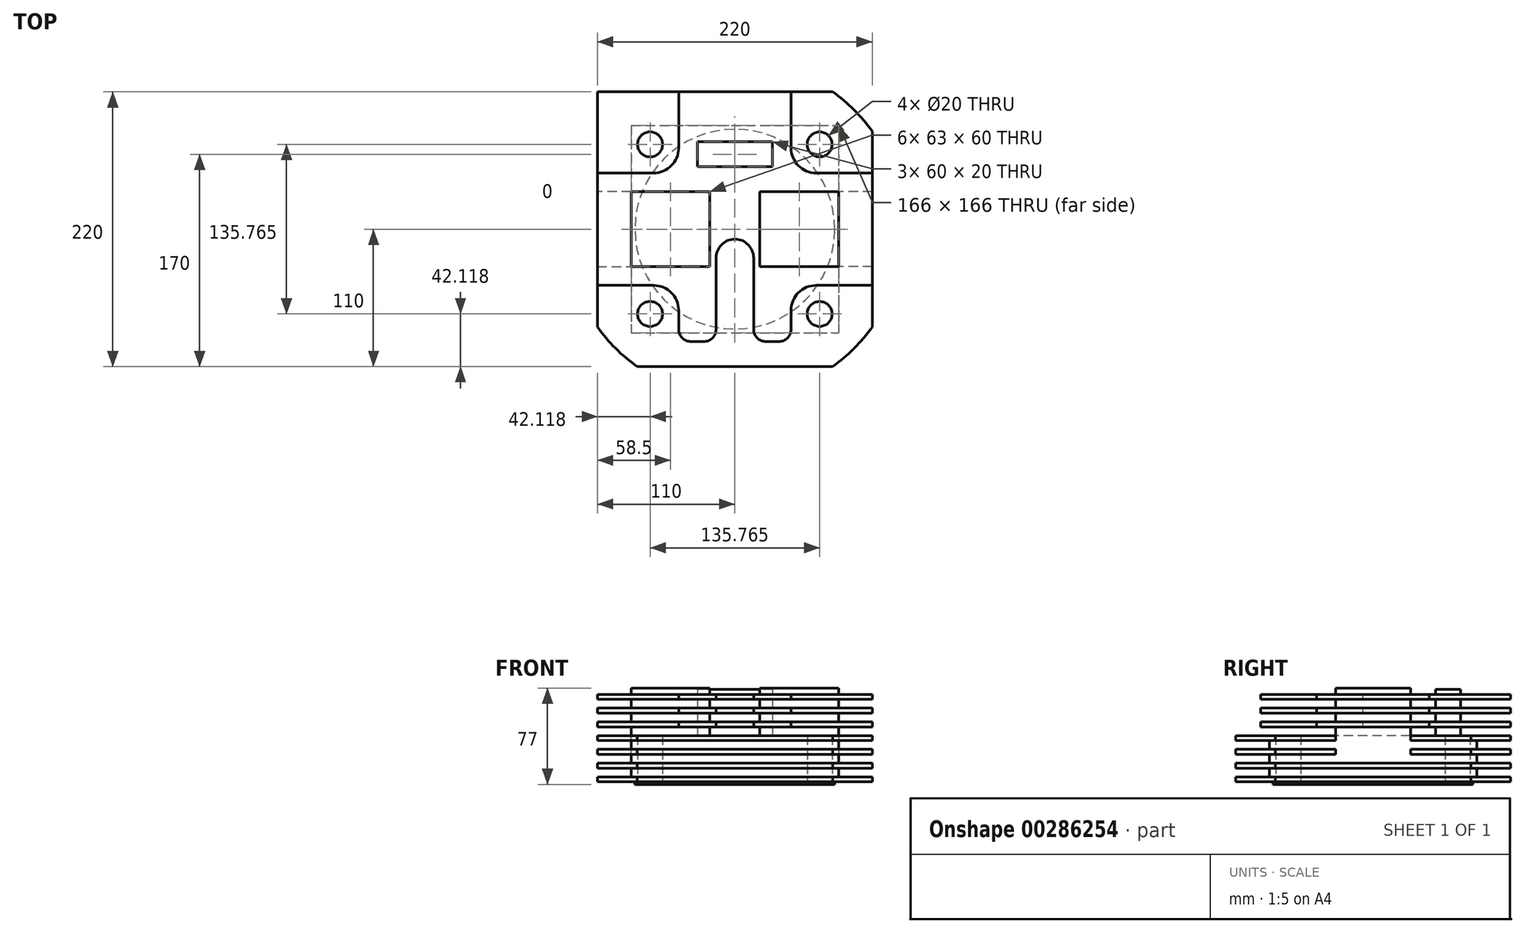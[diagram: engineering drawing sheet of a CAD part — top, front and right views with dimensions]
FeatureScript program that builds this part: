
annotation { "Feature Type Name" : "Feature", "Feature Type Description" : "" }
export const myFeature = defineFeature(function(context is Context, id is Id, definition is map)
    precondition{}
    {
        {
            var Q0;
            Q0=qCreatedBy(makeId("Top.planeOp"),FACE);
            var sketch = newSketch(context, id + "F0", { "sketchPlane" : qUnion([Q0])});
            skLineSegment(sketch, "E0.bottom", {"start": v(-110, 110) * mm, "end": v(110, 110) * mm});
            skLineSegment(sketch, "E0.top", {"start": v(-110, -110) * mm, "end": v(110, -110) * mm});
            skLineSegment(sketch, "E0.left", {"start": v(-110, 110) * mm, "end": v(-110, -110) * mm});
            skLineSegment(sketch, "E0.right", {"start": v(110, 110) * mm, "end": v(110, -110) * mm});
            skSolve(sketch);
        }
        {
            var Q0;
            Q0=makeQuery(id+"F0.imprint","IMPRINT",FACE,{"disambiguationData":[TD([[makeQuery(id+"F0.imprint","IMPRINT",EDGE,{"derivedFrom":sQuery(id+"F0.wireOp",EDGE,"E0.bottom")}),-1.0]])]});
            extrude(context, id + "F1", {"entities" : qUnion([Q0]), "depth" : 4 * mm});
        }
        {
            var Q0;
            Q0=makeQuery(id+"F1.opExtrude","CAP_FACE",FACE,{"disambiguationData":[OSD([sQuery(id+"F0.wireOp",EDGE,"E0.bottom"),sQuery(id+"F0.wireOp",EDGE,"E0.top"),sQuery(id+"F0.wireOp",EDGE,"E0.left"),sQuery(id+"F0.wireOp",EDGE,"E0.right")])],"isStart":false});
            var sketch = newSketch(context, id + "F2", { "sketchPlane" : qUnion([Q0])});
            skLineSegment(sketch, "E1.bottom", {"start": v(-83, 83) * mm, "end": v(83, 83) * mm});
            skLineSegment(sketch, "E1.top", {"start": v(-83, -83) * mm, "end": v(83, -83) * mm});
            skLineSegment(sketch, "E1.left", {"start": v(-83, 83) * mm, "end": v(-83, -83) * mm});
            skLineSegment(sketch, "E1.right", {"start": v(83, 83) * mm, "end": v(83, -83) * mm});
            skSolve(sketch);
        }
        {
            var Q0;
            Q0=makeQuery(id+"F2.imprint","IMPRINT",FACE,{"disambiguationData":[TD([[makeQuery(id+"F2.imprint","IMPRINT",EDGE,{"derivedFrom":sQuery(id+"F2.wireOp",EDGE,"E1.bottom")}),-1.0]])]});
            extrude(context, id + "F3", {"entities" : qUnion([Q0]), "operationType" : NewBodyOperationType.ADD, "depth" : 7 * mm});
        }
        {
            var Q0;
            Q0=makeQuery(id+"F1.opExtrude","CAP_FACE",FACE,{"disambiguationData":[OSD([sQuery(id+"F0.wireOp",EDGE,"E0.bottom"),sQuery(id+"F0.wireOp",EDGE,"E0.top"),sQuery(id+"F0.wireOp",EDGE,"E0.left"),sQuery(id+"F0.wireOp",EDGE,"E0.right")])],"isStart":true});
            var sketch = newSketch(context, id + "F4", { "sketchPlane" : qUnion([Q0])});
            skCircle(sketch, "E2", {"center": v(0, 0) * mm, "radius": 80 * mm});
            skLineSegment(sketch, "E3", {"start": v(0, 0) * mm, "end": v(-75.9, 75.9) * mm});
            skCircle(sketch, "E4", {"center": v(-67.88, 67.88) * mm, "radius": 10 * mm});
            skCircle(sketch, "E5.1.0", {"center": v(-67.88, -67.88) * mm, "radius": 10 * mm});
            skCircle(sketch, "E5.2.0", {"center": v(67.88, -67.88) * mm, "radius": 10 * mm});
            skCircle(sketch, "E5.3.0", {"center": v(67.88, 67.88) * mm, "radius": 10 * mm});
            skSolve(sketch);
        }
        {
            var Q0;
            Q0=makeQuery(id+"F4.imprint","IMPRINT",FACE,{"disambiguationData":[TD([[makeQuery(id+"F4.imprint","IMPRINT",EDGE,{"derivedFrom":sQuery(id+"F4.wireOp",EDGE,"E2")}),1.0]])]});
            extrude(context, id + "F5", {"entities" : qUnion([Q0]), "operationType" : NewBodyOperationType.ADD, "depth" : 2 * mm});
        }
        {
            var Q0;
            Q0=makeQuery(id+"F3.opExtrude","CAP_FACE",FACE,{"disambiguationData":[OSD([sQuery(id+"F2.wireOp",EDGE,"E1.bottom"),sQuery(id+"F2.wireOp",EDGE,"E1.top"),sQuery(id+"F2.wireOp",EDGE,"E1.left"),sQuery(id+"F2.wireOp",EDGE,"E1.right")])],"isStart":false});
            var sketch = newSketch(context, id + "F6", { "sketchPlane" : qUnion([Q0])});
            skLineSegment(sketch, "E6.0", {"start": v(110, 110) * mm, "end": v(110, -110) * mm});
            skLineSegment(sketch, "E6.1", {"start": v(-110, 110) * mm, "end": v(110, 110) * mm});
            skLineSegment(sketch, "E6.2", {"start": v(-110, 110) * mm, "end": v(-110, -110) * mm});
            skLineSegment(sketch, "E6.3", {"start": v(-110, -110) * mm, "end": v(110, -110) * mm});
            skSolve(sketch);
        }
        {
            var Q0;
            Q0=makeQuery(id+"F6.imprint","IMPRINT",FACE,{"disambiguationData":[TD([[makeQuery(id+"F6.imprint","IMPRINT",EDGE,{"derivedFrom":sQuery(id+"F6.wireOp",EDGE,"E6.0")}),-1.0]])]});
            var Q1;
            Q1=makeQuery(id+"F6.imprint","IMPRINT",FACE,{"disambiguationData":[TD([[makeQuery(id+"F6.imprint","IMPRINT",EDGE,{"derivedFrom":makeQuery(id+"F3.opExtrude","CAP_EDGE",EDGE,{"disambiguationData":[OSD([sQuery(id+"F2.wireOp",EDGE,"E1.bottom")])],"isStart":false})}),-1.0]])]});
            extrude(context, id + "F7", {"entities" : qUnion([Q0, Q1]), "operationType" : NewBodyOperationType.ADD, "depth" : 4 * mm});
        }
        {
            var Q0;
            Q0=makeQuery(id+"F7.opExtrude","CAP_FACE",FACE,{"disambiguationData":[OSD([sQuery(id+"F6.wireOp",EDGE,"E6.0"),sQuery(id+"F6.wireOp",EDGE,"E6.1"),sQuery(id+"F6.wireOp",EDGE,"E6.2"),sQuery(id+"F6.wireOp",EDGE,"E6.3")])],"isStart":false});
            var sketch = newSketch(context, id + "F8", { "sketchPlane" : qUnion([Q0])});
            skLineSegment(sketch, "E7.0", {"start": v(-83, -83) * mm, "end": v(83, -83) * mm});
            skLineSegment(sketch, "E7.1", {"start": v(83, 83) * mm, "end": v(83, -83) * mm});
            skLineSegment(sketch, "E7.2", {"start": v(-83, 83) * mm, "end": v(83, 83) * mm});
            skLineSegment(sketch, "E7.3", {"start": v(-83, 83) * mm, "end": v(-83, -83) * mm});
            skSolve(sketch);
        }
        {
            var Q0;
            Q0=makeQuery(id+"F8.imprint","IMPRINT",FACE,{"disambiguationData":[TD([[makeQuery(id+"F8.imprint","IMPRINT",EDGE,{"derivedFrom":sQuery(id+"F8.wireOp",EDGE,"E7.0")}),1.0]])]});
            extrude(context, id + "F9", {"entities" : qUnion([Q0]), "operationType" : NewBodyOperationType.ADD, "depth" : 7 * mm});
        }
        {
            var Q0;
            Q0=makeQuery(id+"F9.opExtrude","CAP_FACE",FACE,{"disambiguationData":[OSD([sQuery(id+"F8.wireOp",EDGE,"E7.0"),sQuery(id+"F8.wireOp",EDGE,"E7.1"),sQuery(id+"F8.wireOp",EDGE,"E7.2"),sQuery(id+"F8.wireOp",EDGE,"E7.3")])],"isStart":false});
            var sketch = newSketch(context, id + "F10", { "sketchPlane" : qUnion([Q0])});
            skLineSegment(sketch, "E8.0", {"start": v(-110, -110) * mm, "end": v(110, -110) * mm});
            skLineSegment(sketch, "E9.0", {"start": v(110, 110) * mm, "end": v(110, -110) * mm});
            skLineSegment(sketch, "E10.0", {"start": v(-110, 110) * mm, "end": v(-110, -110) * mm});
            skLineSegment(sketch, "E11.0", {"start": v(-110, 110) * mm, "end": v(110, 110) * mm});
            skSolve(sketch);
        }
        {
            var Q0;
            Q0=makeQuery(id+"F10.imprint","IMPRINT",FACE,{"disambiguationData":[TD([[makeQuery(id+"F10.imprint","IMPRINT",EDGE,{"derivedFrom":makeQuery(id+"F9.opExtrude","CAP_EDGE",EDGE,{"disambiguationData":[OSD([sQuery(id+"F8.wireOp",EDGE,"E7.0")])],"isStart":false})}),1.0]])]});
            var Q1;
            Q1=makeQuery(id+"F10.imprint","IMPRINT",FACE,{"disambiguationData":[TD([[makeQuery(id+"F10.imprint","IMPRINT",EDGE,{"derivedFrom":sQuery(id+"F10.wireOp",EDGE,"E8.0")}),1.0]])]});
            extrude(context, id + "F11", {"entities" : qUnion([Q0, Q1]), "operationType" : NewBodyOperationType.ADD, "depth" : 4 * mm});
        }
        {
            var Q0;
            Q0=makeQuery(id+"F11.opExtrude","CAP_FACE",FACE,{"disambiguationData":[OSD([sQuery(id+"F10.wireOp",EDGE,"E8.0"),sQuery(id+"F10.wireOp",EDGE,"E9.0"),sQuery(id+"F10.wireOp",EDGE,"E10.0"),sQuery(id+"F10.wireOp",EDGE,"E11.0")])],"isStart":false});
            var sketch = newSketch(context, id + "F12", { "sketchPlane" : qUnion([Q0])});
            skLineSegment(sketch, "E12.bottom", {"start": v(83, -30) * mm, "end": v(-83, -30) * mm});
            skLineSegment(sketch, "E12.top", {"start": v(83, 30) * mm, "end": v(-83, 30) * mm});
            skLineSegment(sketch, "E13.0", {"start": v(83, 83) * mm, "end": v(83, -83) * mm});
            skLineSegment(sketch, "E14.0", {"start": v(-83, 83) * mm, "end": v(-83, -83) * mm});
            skSolve(sketch);
        }
        {
            var Q0;
            Q0=makeQuery(id+"F12.imprint","IMPRINT",FACE,{"disambiguationData":[TD([[makeQuery(id+"F12.imprint","IMPRINT",EDGE,{"derivedFrom":sQuery(id+"F12.wireOp",EDGE,"E12.bottom")}),-1.0]])]});
            extrude(context, id + "F13", {"entities" : qUnion([Q0]), "operationType" : NewBodyOperationType.ADD, "depth" : 49 * mm});
        }
        {
            var Q0;
            Q0=makeQuery(id+"F13.opExtrude","SWEPT_FACE",FACE,{"disambiguationData":[OSD([sQuery(id+"F12.wireOp",EDGE,"E13.0")])]});
            var sketch = newSketch(context, id + "F14", { "sketchPlane" : qUnion([Q0])});
            skLineSegment(sketch, "E15.bottom", {"start": v(-30, 75) * mm, "end": v(30, 75) * mm});
            skLineSegment(sketch, "E15.top", {"start": v(-30, 75) * mm, "end": v(30, 75) * mm});
            skLineSegment(sketch, "E15.left", {"start": v(-30, 75) * mm, "end": v(-30, 75) * mm});
            skLineSegment(sketch, "E15.right", {"start": v(30, 75) * mm, "end": v(30, 75) * mm});
            skLineSegment(sketch, "E16", {"start": v(-30, 75) * mm, "end": v(-30, 15) * mm});
            skLineSegment(sketch, "E17", {"start": v(-30, 15) * mm, "end": v(30, 15) * mm});
            skLineSegment(sketch, "E18", {"start": v(30, 15) * mm, "end": v(30, 75) * mm});
            skSolve(sketch);
        }
        {
            var Q0;
            {var subQ0=sQuery(id+"F14.wireOp",EDGE,"E15.top");Q0=makeQuery(id+"F14.imprint","IMPRINT",FACE,{"disambiguationData":[TD([[makeQuery(id+"F14.imprint","IMPRINT",EDGE,{"derivedFrom":subQ0}),1.0]])]});}
            var Q1;
            {var subQ2=sQuery(id+"F14.wireOp",EDGE,"E17");Q1=makeQuery(id+"F14.imprint","IMPRINT",FACE,{"disambiguationData":[TD([[makeQuery(id+"F14.imprint","IMPRINT",EDGE,{"derivedFrom":subQ2}),1.0]])]});}
            extrude(context, id + "F15", {"entities" : qUnion([Q0, Q1]), "operationType" : NewBodyOperationType.REMOVE, "depth" : 30 * mm});
        }
        {
            var Q0;
            Q0=makeQuery(id+"F11.opExtrude","CAP_FACE",FACE,{"disambiguationData":[OSD([sQuery(id+"F10.wireOp",EDGE,"E8.0"),sQuery(id+"F10.wireOp",EDGE,"E9.0"),sQuery(id+"F10.wireOp",EDGE,"E10.0"),sQuery(id+"F10.wireOp",EDGE,"E11.0")])],"isStart":false});
            var sketch = newSketch(context, id + "F16", { "sketchPlane" : qUnion([Q0])});
            skLineSegment(sketch, "E19.0", {"start": v(-83, 83) * mm, "end": v(-83, -83) * mm});
            skLineSegment(sketch, "E19.1", {"start": v(-83, -83) * mm, "end": v(83, -83) * mm});
            skLineSegment(sketch, "E19.2", {"start": v(83, 83) * mm, "end": v(83, -83) * mm});
            skLineSegment(sketch, "E19.3", {"start": v(-83, 83) * mm, "end": v(83, 83) * mm});
            skSolve(sketch);
        }
        {
            var Q0;
            {var subQ2=sQuery(id+"F16.wireOp",EDGE,"E19.1");Q0=makeQuery(id+"F16.imprint","IMPRINT",FACE,{"disambiguationData":[TD([[makeQuery(id+"F16.imprint","IMPRINT",EDGE,{"derivedFrom":subQ2}),1.0]])]});}
            var Q1;
            {var subQ2=sQuery(id+"F16.wireOp",EDGE,"E19.3");Q1=makeQuery(id+"F16.imprint","IMPRINT",FACE,{"disambiguationData":[TD([[makeQuery(id+"F16.imprint","IMPRINT",EDGE,{"derivedFrom":subQ2}),-1.0]])]});}
            extrude(context, id + "F17", {"entities" : qUnion([Q0, Q1]), "operationType" : NewBodyOperationType.ADD, "depth" : 7 * mm});
        }
        {
            var Q0;
            {var subQ0=sQuery(id+"F16.wireOp",EDGE,"E19.0");Q0=makeQuery(id+"F17.boolean.opBoolean","MERGE",FACE,{"derivedFrom":[makeQuery(id+"F13.opExtrude","SWEPT_FACE",FACE,{"disambiguationData":[OSD([sQuery(id+"F12.wireOp",EDGE,"E14.0")])]}),makeQuery(id+"F17.opExtrude","SWEPT_FACE",FACE,{"disambiguationData":[OSD([subQ0]),TDD([makeQuery(id+"F16.imprint","IMPRINT",EDGE,{"disambiguationData":[TD([[makeQuery(id+"F16.imprint","INTERSECT",VERTEX,{"derivedFrom":[makeQuery(id+"F13.opExtrude","CAP_EDGE",EDGE,{"disambiguationData":[OSD([sQuery(id+"F12.wireOp",EDGE,"E12.top")])],"isStart":true}),subQ0]}),1.0]])],"derivedFrom":subQ0})])]}),makeQuery(id+"F17.opExtrude","SWEPT_FACE",FACE,{"disambiguationData":[OSD([subQ0]),TDD([makeQuery(id+"F16.imprint","IMPRINT",EDGE,{"disambiguationData":[TD([[makeQuery(id+"F16.imprint","INTERSECT",VERTEX,{"derivedFrom":[makeQuery(id+"F13.opExtrude","CAP_EDGE",EDGE,{"disambiguationData":[OSD([sQuery(id+"F12.wireOp",EDGE,"E12.bottom")])],"isStart":true}),subQ0]}),-1.0]])],"derivedFrom":subQ0})])]})]});}
            var sketch = newSketch(context, id + "F18", { "sketchPlane" : qUnion([Q0])});
            skLineSegment(sketch, "E20.0", {"start": v(-30, 15) * mm, "end": v(-30, 75) * mm});
            skLineSegment(sketch, "E20.1", {"start": v(30, 75) * mm, "end": v(-30, 75) * mm});
            skLineSegment(sketch, "E20.2", {"start": v(30, 75) * mm, "end": v(30, 15) * mm});
            skLineSegment(sketch, "E20.3", {"start": v(30, 15) * mm, "end": v(-30, 15) * mm});
            skSolve(sketch);
        }
        {
            var Q0;
            Q0=qSketchRegion(id+"F18",true);
            extrude(context, id + "F19", {"entities" : qUnion([Q0]), "operationType" : NewBodyOperationType.REMOVE, "depth" : 30 * mm});
        }
        {
            var Q0;
            Q0=makeQuery(id+"F17.opExtrude","CAP_FACE",FACE,{"disambiguationData":[OSD([sQuery(id+"F12.wireOp",EDGE,"E12.top"),sQuery(id+"F16.wireOp",EDGE,"E19.0"),sQuery(id+"F16.wireOp",EDGE,"E19.2"),sQuery(id+"F16.wireOp",EDGE,"E19.3")])],"isStart":false});
            var sketch = newSketch(context, id + "F20", { "sketchPlane" : qUnion([Q0])});
            skLineSegment(sketch, "E21.0.0", {"start": v(-110, 30) * mm, "end": v(-83, 30) * mm});
            skLineSegment(sketch, "E21.0.1", {"start": v(-83, 30) * mm, "end": v(-83, 83) * mm});
            skLineSegment(sketch, "E21.0.2", {"start": v(-83, 83) * mm, "end": v(83, 83) * mm});
            skLineSegment(sketch, "E21.0.3", {"start": v(83, 83) * mm, "end": v(83, 30) * mm});
            skLineSegment(sketch, "E21.0.4", {"start": v(83, 30) * mm, "end": v(110, 30) * mm});
            skLineSegment(sketch, "E21.0.5", {"start": v(110, 30) * mm, "end": v(110, 110) * mm});
            skLineSegment(sketch, "E21.0.6", {"start": v(110, 110) * mm, "end": v(-110, 110) * mm});
            skLineSegment(sketch, "E21.0.7", {"start": v(-110, 110) * mm, "end": v(-110, 30) * mm});
            skLineSegment(sketch, "E22.0.0", {"start": v(-83, -30) * mm, "end": v(-110, -30) * mm});
            skLineSegment(sketch, "E22.0.1", {"start": v(-110, -30) * mm, "end": v(-110, -110) * mm});
            skLineSegment(sketch, "E22.0.2", {"start": v(-110, -110) * mm, "end": v(110, -110) * mm});
            skLineSegment(sketch, "E22.0.3", {"start": v(110, -110) * mm, "end": v(110, -30) * mm});
            skLineSegment(sketch, "E22.0.4", {"start": v(110, -30) * mm, "end": v(83, -30) * mm});
            skLineSegment(sketch, "E22.0.5", {"start": v(83, -30) * mm, "end": v(83, -83) * mm});
            skLineSegment(sketch, "E22.0.6", {"start": v(83, -83) * mm, "end": v(-83, -83) * mm});
            skLineSegment(sketch, "E22.0.7", {"start": v(-83, -83) * mm, "end": v(-83, -30) * mm});
            skSolve(sketch);
        }
        {
            var Q0;
            Q0=makeQuery(id+"F20.imprint","IMPRINT",FACE,{"disambiguationData":[TD([[makeQuery(id+"F20.imprint","IMPRINT",EDGE,{"derivedFrom":sQuery(id+"F20.wireOp",EDGE,"E21.0.0")}),1.0]])]});
            var Q1;
            Q1=makeQuery(id+"F20.imprint","IMPRINT",FACE,{"disambiguationData":[TD([[makeQuery(id+"F20.imprint","IMPRINT",EDGE,{"derivedFrom":sQuery(id+"F20.wireOp",EDGE,"E21.0.1")}),1.0]])]});
            var Q2;
            Q2=makeQuery(id+"F20.imprint","IMPRINT",FACE,{"disambiguationData":[TD([[makeQuery(id+"F20.imprint","IMPRINT",EDGE,{"derivedFrom":sQuery(id+"F20.wireOp",EDGE,"E22.0.0")}),1.0]])]});
            var Q3;
            Q3=makeQuery(id+"F17.opExtrude","CAP_FACE",FACE,{"disambiguationData":[OSD([sQuery(id+"F12.wireOp",EDGE,"E12.bottom"),sQuery(id+"F16.wireOp",EDGE,"E19.0"),sQuery(id+"F16.wireOp",EDGE,"E19.1"),sQuery(id+"F16.wireOp",EDGE,"E19.2")])],"isStart":false});
            extrude(context, id + "F21", {"entities" : qUnion([Q0, Q1, Q2, Q3]), "operationType" : NewBodyOperationType.ADD, "depth" : 4 * mm});
        }
        {
            var Q0;
            Q0=makeQuery(id+"F13.opExtrude","SWEPT_FACE",FACE,{"disambiguationData":[OSD([sQuery(id+"F12.wireOp",EDGE,"E12.bottom")])]});
            var sketch = newSketch(context, id + "F22", { "sketchPlane" : qUnion([Q0])});
            skLineSegment(sketch, "E23.0", {"start": v(-110, 37) * mm, "end": v(110, 37) * mm});
            skLineSegment(sketch, "E24", {"start": v(-20, 37) * mm, "end": v(-20, 93.04) * mm});
            skLineSegment(sketch, "E25", {"start": v(-20, 93.04) * mm, "end": v(20, 93.04) * mm});
            skLineSegment(sketch, "E26", {"start": v(20, 93.04) * mm, "end": v(20, 37) * mm});
            skSolve(sketch);
        }
        {
            var Q0;
            {var subQ0=sQuery(id+"F22.wireOp",EDGE,"E24");var subQ1=sQuery(id+"F22.wireOp",EDGE,"E23.0");var subQ2=makeQuery(id+"F22.imprint","INTERSECT",VERTEX,{"derivedFrom":[subQ1,subQ0]});Q0=makeQuery(id+"F22.imprint","IMPRINT",FACE,{"disambiguationData":[TD([[makeQuery(id+"F22.imprint","IMPRINT",EDGE,{"disambiguationData":[TD([[subQ2,1.0]])],"derivedFrom":subQ1}),-1.0]])]});}
            extrude(context, id + "F23", {"entities" : qUnion([Q0]), "operationType" : NewBodyOperationType.REMOVE, "oppositeDirection" : true, "depth" : 60 * mm});
        }
        {
            var Q0;
            Q0=makeQuery(id+"F23.boolean.opBoolean","MERGE",FACE,{"derivedFrom":[makeQuery(id+"F21.opExtrude","CAP_FACE",FACE,{"disambiguationData":[OSD([sQuery(id+"F12.wireOp",EDGE,"E12.top"),sQuery(id+"F20.wireOp",EDGE,"E21.0.0"),sQuery(id+"F20.wireOp",EDGE,"E21.0.4"),sQuery(id+"F20.wireOp",EDGE,"E21.0.5"),sQuery(id+"F20.wireOp",EDGE,"E21.0.6"),sQuery(id+"F20.wireOp",EDGE,"E21.0.7")])],"isStart":false}),makeQuery(id+"F21.boolean.opBoolean","MERGE",FACE,{"derivedFrom":[makeQuery(id+"F21.opExtrude","CAP_FACE",FACE,{"disambiguationData":[OSD([sQuery(id+"F12.wireOp",EDGE,"E12.bottom"),sQuery(id+"F16.wireOp",EDGE,"E19.0"),sQuery(id+"F16.wireOp",EDGE,"E19.1"),sQuery(id+"F16.wireOp",EDGE,"E19.2")])],"isStart":false}),makeQuery(id+"F21.opExtrude","CAP_FACE",FACE,{"disambiguationData":[OSD([sQuery(id+"F20.wireOp",EDGE,"E22.0.0"),sQuery(id+"F20.wireOp",EDGE,"E22.0.1"),sQuery(id+"F20.wireOp",EDGE,"E22.0.2"),sQuery(id+"F20.wireOp",EDGE,"E22.0.3"),sQuery(id+"F20.wireOp",EDGE,"E22.0.4"),sQuery(id+"F20.wireOp",EDGE,"E22.0.5"),sQuery(id+"F20.wireOp",EDGE,"E22.0.6"),sQuery(id+"F20.wireOp",EDGE,"E22.0.7")])],"isStart":false})]}),makeQuery(id+"F23.opExtrude","SWEPT_FACE",FACE,{"disambiguationData":[OSD([sQuery(id+"F22.wireOp",EDGE,"E23.0")])]})]});
            var sketch = newSketch(context, id + "F24", { "sketchPlane" : qUnion([Q0])});
            skLineSegment(sketch, "E27.bottom", {"start": v(30, 70) * mm, "end": v(-30, 70) * mm});
            skLineSegment(sketch, "E27.top", {"start": v(30, 50) * mm, "end": v(-30, 50) * mm});
            skLineSegment(sketch, "E27.left", {"start": v(30, 70) * mm, "end": v(30, 50) * mm});
            skLineSegment(sketch, "E27.right", {"start": v(-30, 70) * mm, "end": v(-30, 50) * mm});
            skSolve(sketch);
        }
        {
            var Q0;
            Q0=makeQuery(id+"F24.imprint","IMPRINT",FACE,{"disambiguationData":[TD([[makeQuery(id+"F24.imprint","IMPRINT",EDGE,{"derivedFrom":sQuery(id+"F24.wireOp",EDGE,"E27.bottom")}),1.0]])]});
            extrude(context, id + "F25", {"entities" : qUnion([Q0]), "operationType" : NewBodyOperationType.ADD, "depth" : 7 * mm});
        }
        {
            var Q0;
            Q0=makeQuery(id+"F25.opExtrude","CAP_FACE",FACE,{"disambiguationData":[OSD([sQuery(id+"F24.wireOp",EDGE,"E27.bottom"),sQuery(id+"F24.wireOp",EDGE,"E27.top"),sQuery(id+"F24.wireOp",EDGE,"E27.left"),sQuery(id+"F24.wireOp",EDGE,"E27.right")])],"isStart":false});
            var sketch = newSketch(context, id + "F26", { "sketchPlane" : qUnion([Q0])});
            skLineSegment(sketch, "E28.0", {"start": v(110, 110) * mm, "end": v(110, -110) * mm});
            skLineSegment(sketch, "E28.1", {"start": v(-110, -110) * mm, "end": v(110, -110) * mm});
            skLineSegment(sketch, "E28.2", {"start": v(-110, 110) * mm, "end": v(-110, -110) * mm});
            skLineSegment(sketch, "E28.3", {"start": v(-110, 110) * mm, "end": v(110, 110) * mm});
            skSolve(sketch);
        }
        {
            var Q0;
            Q0=makeQuery(id+"F26.imprint","IMPRINT",FACE,{"disambiguationData":[TD([[makeQuery(id+"F26.imprint","IMPRINT",EDGE,{"derivedFrom":sQuery(id+"F26.wireOp",EDGE,"E28.0")}),-1.0]])]});
            var Q1;
            Q1=makeQuery(id+"F26.imprint","IMPRINT",FACE,{"disambiguationData":[TD([[makeQuery(id+"F26.imprint","IMPRINT",EDGE,{"derivedFrom":makeQuery(id+"F25.opExtrude","CAP_EDGE",EDGE,{"disambiguationData":[OSD([sQuery(id+"F24.wireOp",EDGE,"E27.bottom")])],"isStart":false})}),1.0]])]});
            extrude(context, id + "F27", {"entities" : qUnion([Q0, Q1]), "operationType" : NewBodyOperationType.ADD, "depth" : 4 * mm});
        }
        {
            var Q0;
            Q0=makeQuery(id+"F27.opExtrude","CAP_FACE",FACE,{"disambiguationData":[OSD([sQuery(id+"F26.wireOp",EDGE,"E28.0"),sQuery(id+"F26.wireOp",EDGE,"E28.1"),sQuery(id+"F26.wireOp",EDGE,"E28.2"),sQuery(id+"F26.wireOp",EDGE,"E28.3")])],"isStart":false});
            var sketch = newSketch(context, id + "F28", { "sketchPlane" : qUnion([Q0])});
            skLineSegment(sketch, "E29.0", {"start": v(30, 70) * mm, "end": v(30, 50) * mm});
            skLineSegment(sketch, "E29.1", {"start": v(30, 50) * mm, "end": v(-30, 50) * mm});
            skLineSegment(sketch, "E29.2", {"start": v(30, 70) * mm, "end": v(-30, 70) * mm});
            skLineSegment(sketch, "E29.3", {"start": v(-30, 70) * mm, "end": v(-30, 50) * mm});
            skSolve(sketch);
        }
        {
            var Q0;
            Q0=makeQuery(id+"F28.imprint","IMPRINT",FACE,{"disambiguationData":[TD([[makeQuery(id+"F28.imprint","IMPRINT",EDGE,{"derivedFrom":sQuery(id+"F28.wireOp",EDGE,"E29.0")}),-1.0]])]});
            extrude(context, id + "F29", {"entities" : qUnion([Q0]), "operationType" : NewBodyOperationType.ADD, "depth" : 7 * mm});
        }
        {
            var Q0;
            Q0=makeQuery(id+"F29.opExtrude","CAP_FACE",FACE,{"disambiguationData":[OSD([sQuery(id+"F28.wireOp",EDGE,"E29.0"),sQuery(id+"F28.wireOp",EDGE,"E29.1"),sQuery(id+"F28.wireOp",EDGE,"E29.2"),sQuery(id+"F28.wireOp",EDGE,"E29.3")])],"isStart":false});
            var sketch = newSketch(context, id + "F30", { "sketchPlane" : qUnion([Q0])});
            skLineSegment(sketch, "E30.0", {"start": v(110, 110) * mm, "end": v(110, -110) * mm});
            skLineSegment(sketch, "E30.1", {"start": v(-110, 110) * mm, "end": v(110, 110) * mm});
            skLineSegment(sketch, "E30.2", {"start": v(-110, -110) * mm, "end": v(110, -110) * mm});
            skLineSegment(sketch, "E30.3", {"start": v(-110, 110) * mm, "end": v(-110, -110) * mm});
            skSolve(sketch);
        }
        {
            var Q0;
            Q0=makeQuery(id+"F30.imprint","IMPRINT",FACE,{"disambiguationData":[TD([[makeQuery(id+"F30.imprint","IMPRINT",EDGE,{"derivedFrom":sQuery(id+"F30.wireOp",EDGE,"E30.0")}),-1.0]])]});
            var Q1;
            Q1=makeQuery(id+"F30.imprint","IMPRINT",FACE,{"disambiguationData":[TD([[makeQuery(id+"F30.imprint","IMPRINT",EDGE,{"derivedFrom":makeQuery(id+"F29.opExtrude","CAP_EDGE",EDGE,{"disambiguationData":[OSD([sQuery(id+"F28.wireOp",EDGE,"E29.0")])],"isStart":false})}),-1.0]])]});
            extrude(context, id + "F31", {"entities" : qUnion([Q0, Q1]), "operationType" : NewBodyOperationType.ADD, "depth" : 4 * mm});
        }
        {
            var Q0;
            Q0=makeQuery(id+"F31.opExtrude","CAP_FACE",FACE,{"disambiguationData":[OSD([sQuery(id+"F30.wireOp",EDGE,"E30.0"),sQuery(id+"F30.wireOp",EDGE,"E30.1"),sQuery(id+"F30.wireOp",EDGE,"E30.2"),sQuery(id+"F30.wireOp",EDGE,"E30.3")])],"isStart":false});
            var sketch = newSketch(context, id + "F32", { "sketchPlane" : qUnion([Q0])});
            skLineSegment(sketch, "E31.0", {"start": v(30, 70) * mm, "end": v(30, 50) * mm});
            skLineSegment(sketch, "E31.1", {"start": v(30, 70) * mm, "end": v(-30, 70) * mm});
            skLineSegment(sketch, "E31.2", {"start": v(-30, 70) * mm, "end": v(-30, 50) * mm});
            skLineSegment(sketch, "E31.3", {"start": v(30, 50) * mm, "end": v(-30, 50) * mm});
            skSolve(sketch);
        }
        {
            var Q0;
            Q0=makeQuery(id+"F32.imprint","IMPRINT",FACE,{"disambiguationData":[TD([[makeQuery(id+"F32.imprint","IMPRINT",EDGE,{"derivedFrom":sQuery(id+"F32.wireOp",EDGE,"E31.0")}),-1.0]])]});
            extrude(context, id + "F33", {"entities" : qUnion([Q0]), "operationType" : NewBodyOperationType.ADD, "depth" : 7 * mm});
        }
        {
            var Q0;
            Q0=makeQuery(id+"F33.opExtrude","CAP_FACE",FACE,{"disambiguationData":[OSD([sQuery(id+"F32.wireOp",EDGE,"E31.0"),sQuery(id+"F32.wireOp",EDGE,"E31.1"),sQuery(id+"F32.wireOp",EDGE,"E31.2"),sQuery(id+"F32.wireOp",EDGE,"E31.3")])],"isStart":false});
            var sketch = newSketch(context, id + "F34", { "sketchPlane" : qUnion([Q0])});
            skLineSegment(sketch, "E32.0", {"start": v(110, 110) * mm, "end": v(110, -110) * mm});
            skLineSegment(sketch, "E32.1", {"start": v(-110, 110) * mm, "end": v(110, 110) * mm});
            skLineSegment(sketch, "E32.2", {"start": v(-110, 110) * mm, "end": v(-110, -110) * mm});
            skLineSegment(sketch, "E32.3", {"start": v(-110, -110) * mm, "end": v(110, -110) * mm});
            skSolve(sketch);
        }
        {
            var Q0;
            Q0=makeQuery(id+"F34.imprint","IMPRINT",FACE,{"disambiguationData":[TD([[makeQuery(id+"F34.imprint","IMPRINT",EDGE,{"derivedFrom":sQuery(id+"F34.wireOp",EDGE,"E32.0")}),-1.0]])]});
            var Q1;
            Q1=makeQuery(id+"F34.imprint","IMPRINT",FACE,{"disambiguationData":[TD([[makeQuery(id+"F34.imprint","IMPRINT",EDGE,{"derivedFrom":makeQuery(id+"F33.opExtrude","CAP_EDGE",EDGE,{"disambiguationData":[OSD([sQuery(id+"F32.wireOp",EDGE,"E31.0")])],"isStart":false})}),-1.0]])]});
            extrude(context, id + "F35", {"entities" : qUnion([Q0, Q1]), "operationType" : NewBodyOperationType.ADD, "depth" : 4 * mm});
        }
        {
            var Q0;
            Q0=makeQuery(id+"F35.opExtrude","CAP_FACE",FACE,{"disambiguationData":[OSD([sQuery(id+"F34.wireOp",EDGE,"E32.0"),sQuery(id+"F34.wireOp",EDGE,"E32.1"),sQuery(id+"F34.wireOp",EDGE,"E32.2"),sQuery(id+"F34.wireOp",EDGE,"E32.3")])],"isStart":false});
            var sketch = newSketch(context, id + "F36", { "sketchPlane" : qUnion([Q0])});
            skLineSegment(sketch, "E33.0", {"start": v(30, 70) * mm, "end": v(30, 50) * mm});
            skLineSegment(sketch, "E33.1", {"start": v(30, 50) * mm, "end": v(-30, 50) * mm});
            skLineSegment(sketch, "E33.2", {"start": v(30, 70) * mm, "end": v(-30, 70) * mm});
            skLineSegment(sketch, "E33.3", {"start": v(-30, 70) * mm, "end": v(-30, 50) * mm});
            skPoint(sketch, "E33.4", {"position": v(30, 60) * mm});
            skSolve(sketch);
        }
        {
            var Q0;
            Q0=makeQuery(id+"F36.imprint","IMPRINT",FACE,{"disambiguationData":[TD([[makeQuery(id+"F36.imprint","IMPRINT",EDGE,{"derivedFrom":sQuery(id+"F36.wireOp",EDGE,"E33.0")}),-1.0]])]});
            extrude(context, id + "F37", {"entities" : qUnion([Q0]), "operationType" : NewBodyOperationType.ADD, "depth" : 4 * mm});
        }
        {
            var Q0;
            Q0=makeQuery(id+"F4.imprint","IMPRINT",FACE,{"disambiguationData":[TD([[makeQuery(id+"F4.imprint","IMPRINT",EDGE,{"derivedFrom":sQuery(id+"F4.wireOp",EDGE,"E2")}),-1.0]])]});
            var sketch = newSketch(context, id + "F38", { "sketchPlane" : qUnion([Q0])});
            skCircle(sketch, "E34", {"center": v(0, 0) * mm, "radius": 135 * mm});
            skCircle(sketch, "E35.0", {"center": v(0, 0) * mm, "radius": 185 * mm});
            skSolve(sketch);
        }
        {
            var Q0;
            {var subQ0=sQuery(id+"F38.wireOp",EDGE,"E34");var subQ1=makeQuery(id+"F4.imprint","IMPRINT",EDGE,{"derivedFrom":makeQuery(id+"F1.opExtrude","CAP_EDGE",EDGE,{"disambiguationData":[OSD([sQuery(id+"F0.wireOp",EDGE,"E0.top")])],"isStart":true})});var subQ2=makeQuery(id+"F38.imprint","INTERSECT",VERTEX,{"disambiguationData":[OD(1.0)],"derivedFrom":[subQ1,subQ0]});Q0=makeQuery(id+"F38.imprint","IMPRINT",FACE,{"disambiguationData":[TD([[makeQuery(id+"F38.imprint","IMPRINT",EDGE,{"disambiguationData":[TD([[subQ2,-1.0]])],"derivedFrom":subQ0}),-1.0]])]});}
            var Q1;
            {var subQ0=sQuery(id+"F38.wireOp",EDGE,"E34");var subQ1=makeQuery(id+"F4.imprint","IMPRINT",EDGE,{"derivedFrom":makeQuery(id+"F1.opExtrude","CAP_EDGE",EDGE,{"disambiguationData":[OSD([sQuery(id+"F0.wireOp",EDGE,"E0.bottom")])],"isStart":true})});var subQ2=makeQuery(id+"F38.imprint","INTERSECT",VERTEX,{"disambiguationData":[OD(1.0)],"derivedFrom":[subQ1,subQ0]});Q1=makeQuery(id+"F38.imprint","IMPRINT",FACE,{"disambiguationData":[TD([[makeQuery(id+"F38.imprint","IMPRINT",EDGE,{"disambiguationData":[TD([[subQ2,-1.0]])],"derivedFrom":subQ0}),-1.0]])]});}
            var Q2;
            {var subQ0=sQuery(id+"F38.wireOp",EDGE,"E34");var subQ1=makeQuery(id+"F4.imprint","IMPRINT",EDGE,{"derivedFrom":makeQuery(id+"F1.opExtrude","CAP_EDGE",EDGE,{"disambiguationData":[OSD([sQuery(id+"F0.wireOp",EDGE,"E0.top")])],"isStart":true})});var subQ2=makeQuery(id+"F38.imprint","INTERSECT",VERTEX,{"disambiguationData":[OD(0.0)],"derivedFrom":[subQ1,subQ0]});Q2=makeQuery(id+"F38.imprint","IMPRINT",FACE,{"disambiguationData":[TD([[makeQuery(id+"F38.imprint","IMPRINT",EDGE,{"disambiguationData":[TD([[subQ2,1.0]])],"derivedFrom":subQ0}),-1.0]])]});}
            var Q3;
            {var subQ0=sQuery(id+"F38.wireOp",EDGE,"E34");var subQ1=makeQuery(id+"F4.imprint","IMPRINT",EDGE,{"derivedFrom":makeQuery(id+"F1.opExtrude","CAP_EDGE",EDGE,{"disambiguationData":[OSD([sQuery(id+"F0.wireOp",EDGE,"E0.left")])],"isStart":true})});var subQ2=makeQuery(id+"F38.imprint","INTERSECT",VERTEX,{"disambiguationData":[OD(1.0)],"derivedFrom":[subQ1,subQ0]});Q3=makeQuery(id+"F38.imprint","IMPRINT",FACE,{"disambiguationData":[TD([[makeQuery(id+"F38.imprint","IMPRINT",EDGE,{"disambiguationData":[TD([[subQ2,-1.0]])],"derivedFrom":subQ0}),-1.0]])]});}
            extrude(context, id + "F39", {"entities" : qUnion([Q0, Q1, Q2, Q3]), "operationType" : NewBodyOperationType.REMOVE, "oppositeDirection" : true, "depth" : 70 * mm});
        }
        {
            var Q0;
            {var subQ0=sQuery(id+"F4.wireOp",EDGE,"E4");var subQ1=sQuery(id+"F4.wireOp",EDGE,"E3");var subQ2=makeQuery(id+"F4.imprint","INTERSECT",VERTEX,{"disambiguationData":[OD(0.0)],"derivedFrom":[subQ1,subQ0]});Q0=makeQuery(id+"F4.imprint","IMPRINT",FACE,{"disambiguationData":[TD([[makeQuery(id+"F4.imprint","IMPRINT",EDGE,{"disambiguationData":[TD([[subQ2,1.0]])],"derivedFrom":subQ1}),1.0]])]});}
            var Q1;
            {var subQ0=sQuery(id+"F4.wireOp",EDGE,"E4");var subQ1=sQuery(id+"F4.wireOp",EDGE,"E3");var subQ2=makeQuery(id+"F4.imprint","INTERSECT",VERTEX,{"disambiguationData":[OD(0.0)],"derivedFrom":[subQ1,subQ0]});Q1=makeQuery(id+"F4.imprint","IMPRINT",FACE,{"disambiguationData":[TD([[makeQuery(id+"F4.imprint","IMPRINT",EDGE,{"disambiguationData":[TD([[subQ2,1.0]])],"derivedFrom":subQ1}),-1.0]])]});}
            var Q2;
            Q2=makeQuery(id+"F4.imprint","IMPRINT",FACE,{"disambiguationData":[TD([[makeQuery(id+"F4.imprint","IMPRINT",EDGE,{"derivedFrom":sQuery(id+"F4.wireOp",EDGE,"E5.1.0")}),1.0]])]});
            var Q3;
            Q3=makeQuery(id+"F4.imprint","IMPRINT",FACE,{"disambiguationData":[TD([[makeQuery(id+"F4.imprint","IMPRINT",EDGE,{"derivedFrom":sQuery(id+"F4.wireOp",EDGE,"E5.3.0")}),1.0]])]});
            var Q4;
            Q4=makeQuery(id+"F4.imprint","IMPRINT",FACE,{"disambiguationData":[TD([[makeQuery(id+"F4.imprint","IMPRINT",EDGE,{"derivedFrom":sQuery(id+"F4.wireOp",EDGE,"E5.2.0")}),1.0]])]});
            extrude(context, id + "F40", {"entities" : qUnion([Q0, Q1, Q2, Q3, Q4]), "operationType" : NewBodyOperationType.REMOVE, "oppositeDirection" : true, "depth" : 100 * mm});
        }
        {
            var Q0;
            {var subQ0=sQuery(id+"F12.wireOp",EDGE,"E13.0");var subQ1=sQuery(id+"F12.wireOp",EDGE,"E12.bottom");var subQ2=sQuery(id+"F12.wireOp",EDGE,"E12.top");Q0=makeQuery(id+"F23.boolean.opBoolean","SPLIT",FACE,{"disambiguationData":[TD([makeQuery(id+"F9.opExtrude","SWEPT_FACE",FACE,{"disambiguationData":[OSD([sQuery(id+"F8.wireOp",EDGE,"E7.1")])]})])],"derivedFrom":makeQuery(id+"F13.opExtrude","CAP_FACE",FACE,{"disambiguationData":[OSD([subQ1,subQ2,subQ0,sQuery(id+"F12.wireOp",EDGE,"E14.0")])],"isStart":false})});}
            cPlane(context, id + "F41", {"entities" : qUnion([Q0]), "cplaneType" : CPlaneType.OFFSET, "offset" : 100 * mm, "width" : 150 * mm, "height" : 150 * mm});
        }
        {
            var Q0;
            Q0=qCreatedBy(id+"F41.planeOp",FACE);
            var sketch = newSketch(context, id + "F42", { "sketchPlane" : qUnion([Q0])});
            skLineSegment(sketch, "E36.bottom", {"start": v(145, -45) * mm, "end": v(65, -45) * mm});
            skLineSegment(sketch, "E36.top", {"start": v(145, -145) * mm, "end": v(45, -145) * mm});
            skLineSegment(sketch, "E36.left", {"start": v(145, -45) * mm, "end": v(145, -145) * mm});
            skLineSegment(sketch, "E36.right", {"start": v(45, -65) * mm, "end": v(45, -80) * mm});
            skLineSegment(sketch, "E37.bottom", {"start": v(-65, -45) * mm, "end": v(-145, -45) * mm});
            skLineSegment(sketch, "E37.top", {"start": v(45, -145) * mm, "end": v(-145, -145) * mm});
            skLineSegment(sketch, "E37.left", {"start": v(-45, -65) * mm, "end": v(-45, -80) * mm});
            skLineSegment(sketch, "E37.right", {"start": v(-145, -45) * mm, "end": v(-145, -145) * mm});
            skPoint(sketch, "E38.visualSharp", {"position": v(45, -45) * mm});
            skArc(sketch, "E38.filletArc", {"start": v(65, -45) * mm, "mid": v(50.86, -50.86) * mm, "end": v(45, -65) * mm});
            skPoint(sketch, "E39.visualSharp", {"position": v(-45, -45) * mm});
            skArc(sketch, "E39.filletArc", {"start": v(-45, -65) * mm, "mid": v(-50.86, -50.86) * mm, "end": v(-65, -45) * mm});
            skLineSegment(sketch, "E40.bottom", {"start": v(-15, -132.63) * mm, "end": v(15, -132.63) * mm});
            skLineSegment(sketch, "E40.left", {"start": v(-15, -80) * mm, "end": v(-15, -23) * mm});
            skLineSegment(sketch, "E40.right", {"start": v(15, -80) * mm, "end": v(15, -23) * mm});
            skArc(sketch, "E41", {"start": v(15, -23) * mm, "mid": v(0, -8) * mm, "end": v(-15, -23) * mm});
            skLineSegment(sketch, "E42", {"start": v(-35, -90) * mm, "end": v(-25, -90) * mm});
            skArc(sketch, "E43.filletArc", {"start": v(-45, -80) * mm, "mid": v(-42.07, -87.07) * mm, "end": v(-35, -90) * mm});
            skArc(sketch, "E44.filletArc", {"start": v(-25, -90) * mm, "mid": v(-17.93, -87.07) * mm, "end": v(-15, -80) * mm});
            skLineSegment(sketch, "E45", {"start": v(35, -90) * mm, "end": v(25, -90) * mm});
            skArc(sketch, "E46.filletArc", {"start": v(15, -80) * mm, "mid": v(17.93, -87.07) * mm, "end": v(25, -90) * mm});
            skPoint(sketch, "E47.newPointB", {"position": v(45, -90) * mm});
            skArc(sketch, "E47.filletArc", {"start": v(35, -90) * mm, "mid": v(42.07, -87.07) * mm, "end": v(45, -80) * mm});
            skPoint(sketch, "E48.orphan", {"position": v(-45, -145) * mm});
            skSolve(sketch);
        }
        {
            var Q0;
            Q0=makeQuery(id+"F42.imprint","IMPRINT",FACE,{"disambiguationData":[TD([[makeQuery(id+"F42.imprint","IMPRINT",EDGE,{"derivedFrom":sQuery(id+"F42.wireOp",EDGE,"E36.bottom")}),1.0]])]});
            extrude(context, id + "F43", {"entities" : qUnion([Q0]), "operationType" : NewBodyOperationType.REMOVE, "oppositeDirection" : true, "depth" : 135 * mm});
        }
        {
            var Q0;
            Q0=qCreatedBy(id+"F41.planeOp",FACE);
            var sketch = newSketch(context, id + "F44", { "sketchPlane" : qUnion([Q0])});
            skLineSegment(sketch, "E49.bottom", {"start": v(132.73, 137.01) * mm, "end": v(45, 137.01) * mm});
            skLineSegment(sketch, "E49.top", {"start": v(132.73, 45) * mm, "end": v(65, 45) * mm});
            skLineSegment(sketch, "E49.left", {"start": v(132.73, 137.01) * mm, "end": v(132.73, 45) * mm});
            skLineSegment(sketch, "E49.right", {"start": v(45, 137.01) * mm, "end": v(45, 65) * mm});
            skLineSegment(sketch, "E50.bottom", {"start": v(-45, 137.01) * mm, "end": v(-153.82, 137.01) * mm});
            skLineSegment(sketch, "E50.top", {"start": v(-65, 45) * mm, "end": v(-153.82, 45) * mm});
            skLineSegment(sketch, "E50.left", {"start": v(-45, 137.01) * mm, "end": v(-45, 65) * mm});
            skLineSegment(sketch, "E50.right", {"start": v(-153.82, 137.01) * mm, "end": v(-153.82, 45) * mm});
            skPoint(sketch, "E51.visualSharp", {"position": v(45, 45) * mm});
            skArc(sketch, "E51.filletArc", {"start": v(45, 65) * mm, "mid": v(50.86, 50.86) * mm, "end": v(65, 45) * mm});
            skPoint(sketch, "E52.visualSharp", {"position": v(-45, 45) * mm});
            skArc(sketch, "E52.filletArc", {"start": v(-65, 45) * mm, "mid": v(-50.86, 50.86) * mm, "end": v(-45, 65) * mm});
            skSolve(sketch);
        }
        {
            var Q0;
            Q0=makeQuery(id+"F44.imprint","IMPRINT",FACE,{"disambiguationData":[TD([[makeQuery(id+"F44.imprint","IMPRINT",EDGE,{"derivedFrom":sQuery(id+"F44.wireOp",EDGE,"E49.bottom")}),1.0]])]});
            var Q1;
            Q1=makeQuery(id+"F44.imprint","IMPRINT",FACE,{"disambiguationData":[TD([[makeQuery(id+"F44.imprint","IMPRINT",EDGE,{"derivedFrom":sQuery(id+"F44.wireOp",EDGE,"E50.bottom")}),1.0]])]});
            extrude(context, id + "F45", {"entities" : qUnion([Q0, Q1]), "operationType" : NewBodyOperationType.REMOVE, "oppositeDirection" : true, "depth" : 135 * mm});
        }
    });
